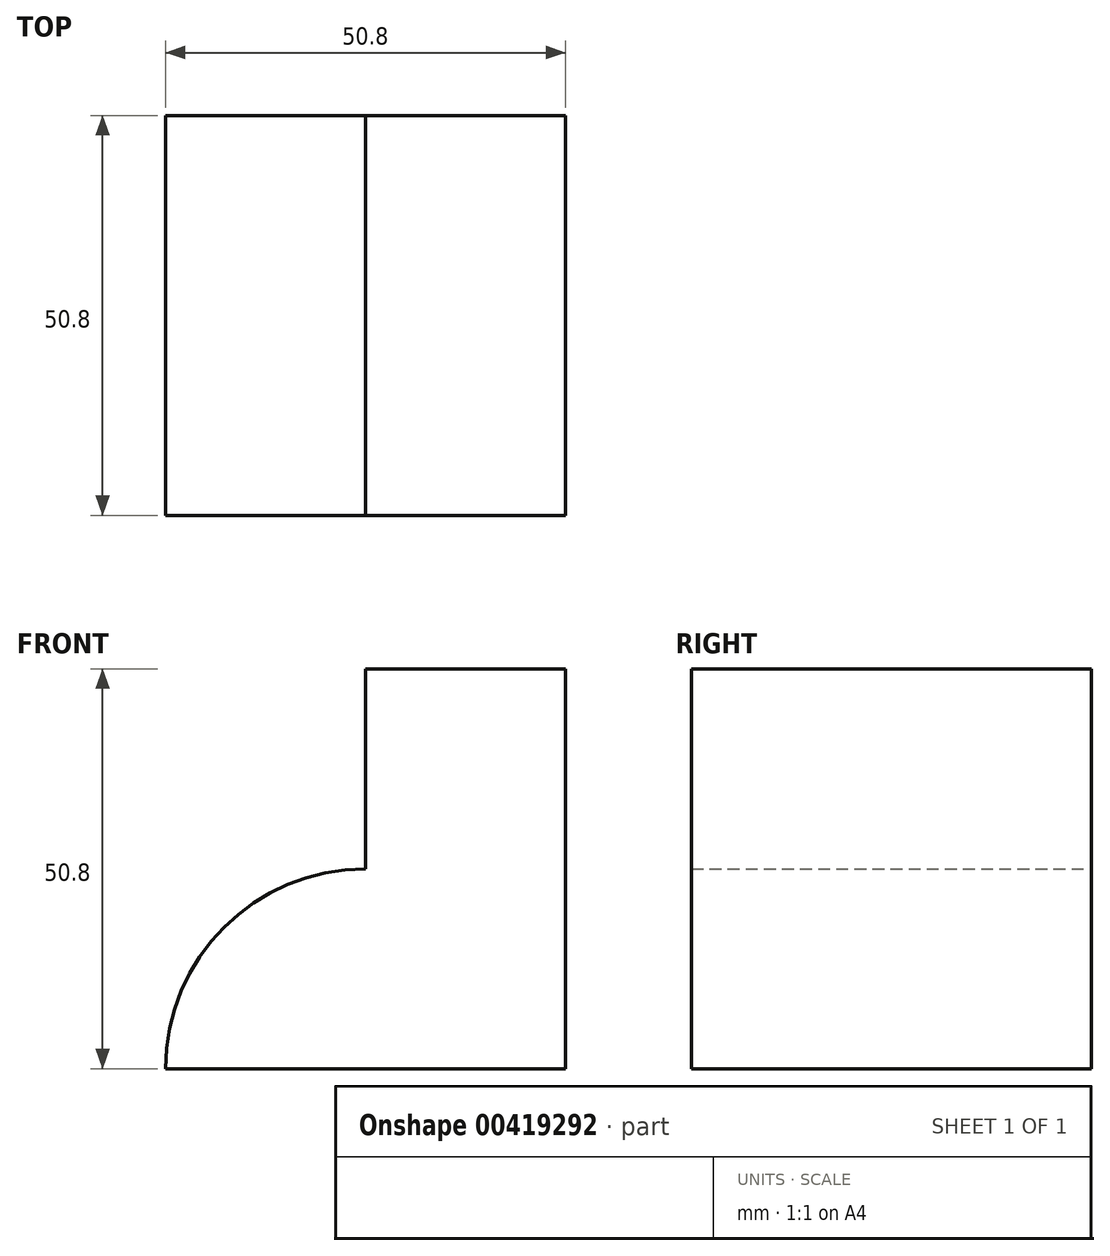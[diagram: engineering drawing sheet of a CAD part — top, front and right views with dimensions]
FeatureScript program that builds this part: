
annotation { "Feature Type Name" : "Feature", "Feature Type Description" : "" }
export const myFeature = defineFeature(function(context is Context, id is Id, definition is map)
    precondition{}
    {
        {
            var Q0;
            Q0=qCreatedBy(makeId("Front.planeOp"),FACE);
            var sketch = newSketch(context, id + "F0", { "sketchPlane" : qUnion([Q0])});
            skLineSegment(sketch, "E0", {"start": v(-50.8, 0) * mm, "end": v(0, 0) * mm});
            skLineSegment(sketch, "E1", {"start": v(0, 0) * mm, "end": v(0, 50.8) * mm});
            skLineSegment(sketch, "E2", {"start": v(0, 50.8) * mm, "end": v(-25.4, 50.8) * mm});
            skLineSegment(sketch, "E3", {"start": v(-25.4, 50.8) * mm, "end": v(-25.4, 25.4) * mm});
            skLineSegment(sketch, "E4", {"start": v(-25.4, 25.4) * mm, "end": v(-25.4, 25.4) * mm});
            skLineSegment(sketch, "E5", {"start": v(-50.8, 0) * mm, "end": v(-50.8, 0) * mm});
            skPoint(sketch, "E6.visualSharp", {"position": v(-50.8, 25.4) * mm});
            skArc(sketch, "E6.filletArc", {"start": v(-25.4, 25.4) * mm, "mid": v(-43.36, 17.96) * mm, "end": v(-50.8, 0) * mm});
            skSolve(sketch);
        }
        {
            var Q0;
            Q0=makeQuery(id+"F0.imprint","IMPRINT",FACE,{"disambiguationData":[TD([[makeQuery(id+"F0.imprint","IMPRINT",EDGE,{"derivedFrom":sQuery(id+"F0.wireOp",EDGE,"E0")}),1.0]])]});
            extrude(context, id + "F1", {"entities" : qUnion([Q0]), "depth" : 50.8 * mm});
        }
    });
